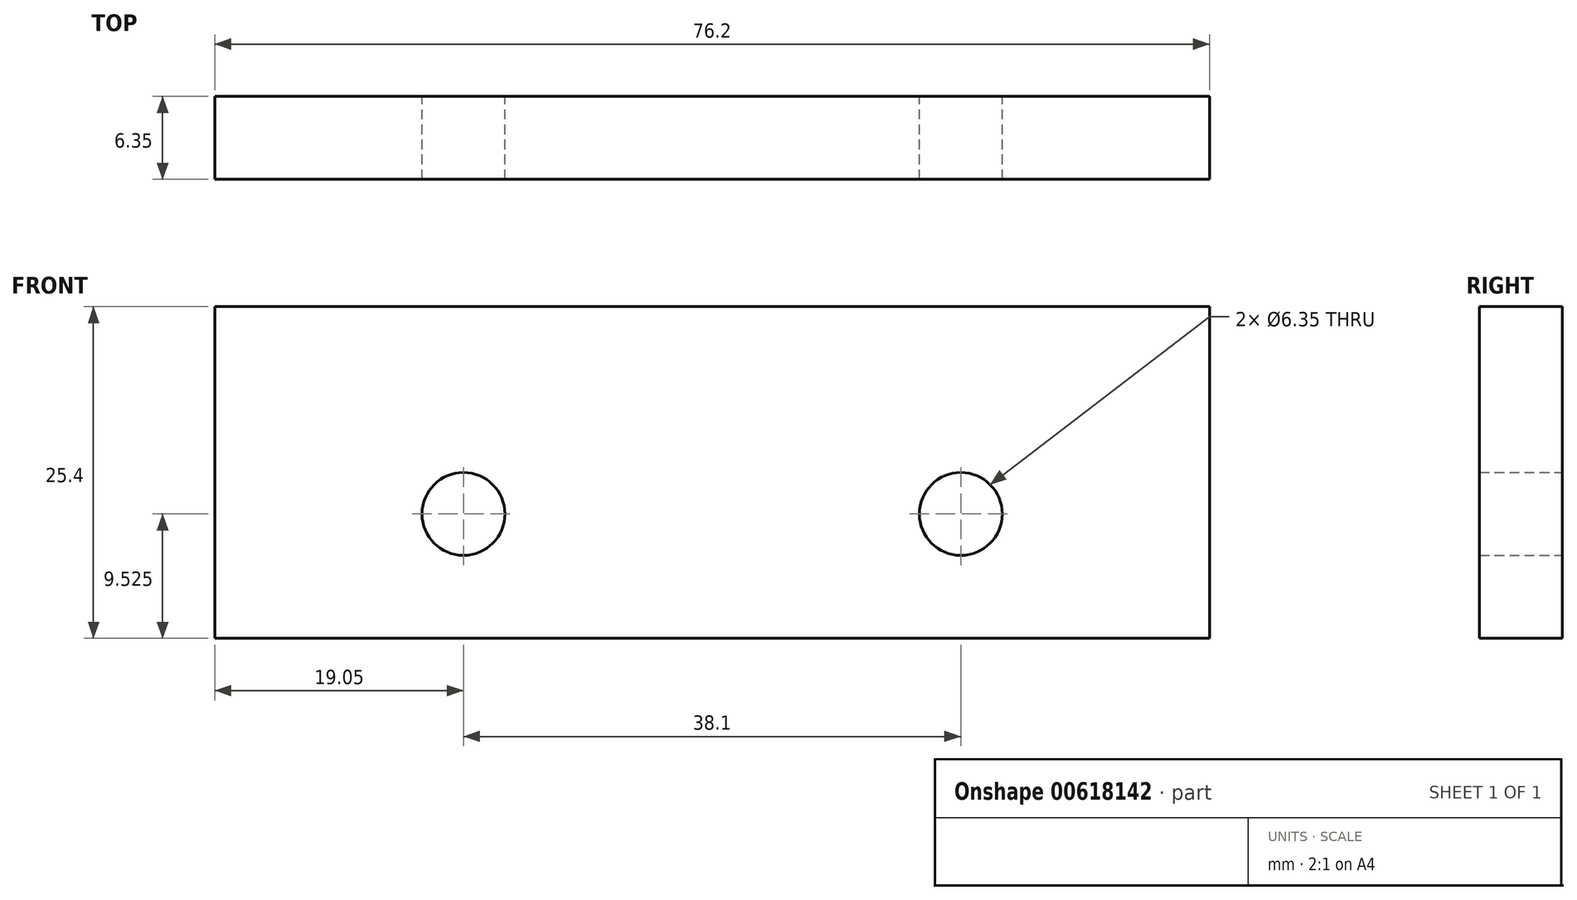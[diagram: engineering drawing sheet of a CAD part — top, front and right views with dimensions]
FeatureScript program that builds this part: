
annotation { "Feature Type Name" : "Feature", "Feature Type Description" : "" }
export const myFeature = defineFeature(function(context is Context, id is Id, definition is map)
    precondition{}
    {
        {
            var Q0;
            Q0=qCreatedBy(makeId("Front.planeOp"),FACE);
            var sketch = newSketch(context, id + "F0", { "sketchPlane" : qUnion([Q0])});
            skLineSegment(sketch, "E0.bottom", {"start": v(0, 0) * mm, "end": v(76.2, 0) * mm});
            skLineSegment(sketch, "E0.top", {"start": v(0, 25.4) * mm, "end": v(76.2, 25.4) * mm});
            skLineSegment(sketch, "E0.left", {"start": v(0, 0) * mm, "end": v(0, 25.4) * mm});
            skLineSegment(sketch, "E0.right", {"start": v(76.2, 0) * mm, "end": v(76.2, 25.4) * mm});
            skCircle(sketch, "E1", {"center": v(19.05, 9.53) * mm, "radius": 3.18 * mm});
            skCircle(sketch, "E2", {"center": v(57.15, 9.53) * mm, "radius": 3.18 * mm});
            skSolve(sketch);
        }
        {
            var Q0;
            Q0=qSketchRegion(id+"F0",true);
            extrude(context, id + "F1", {"entities" : qUnion([Q0]), "depth" : 6.35 * mm});
        }
    });
